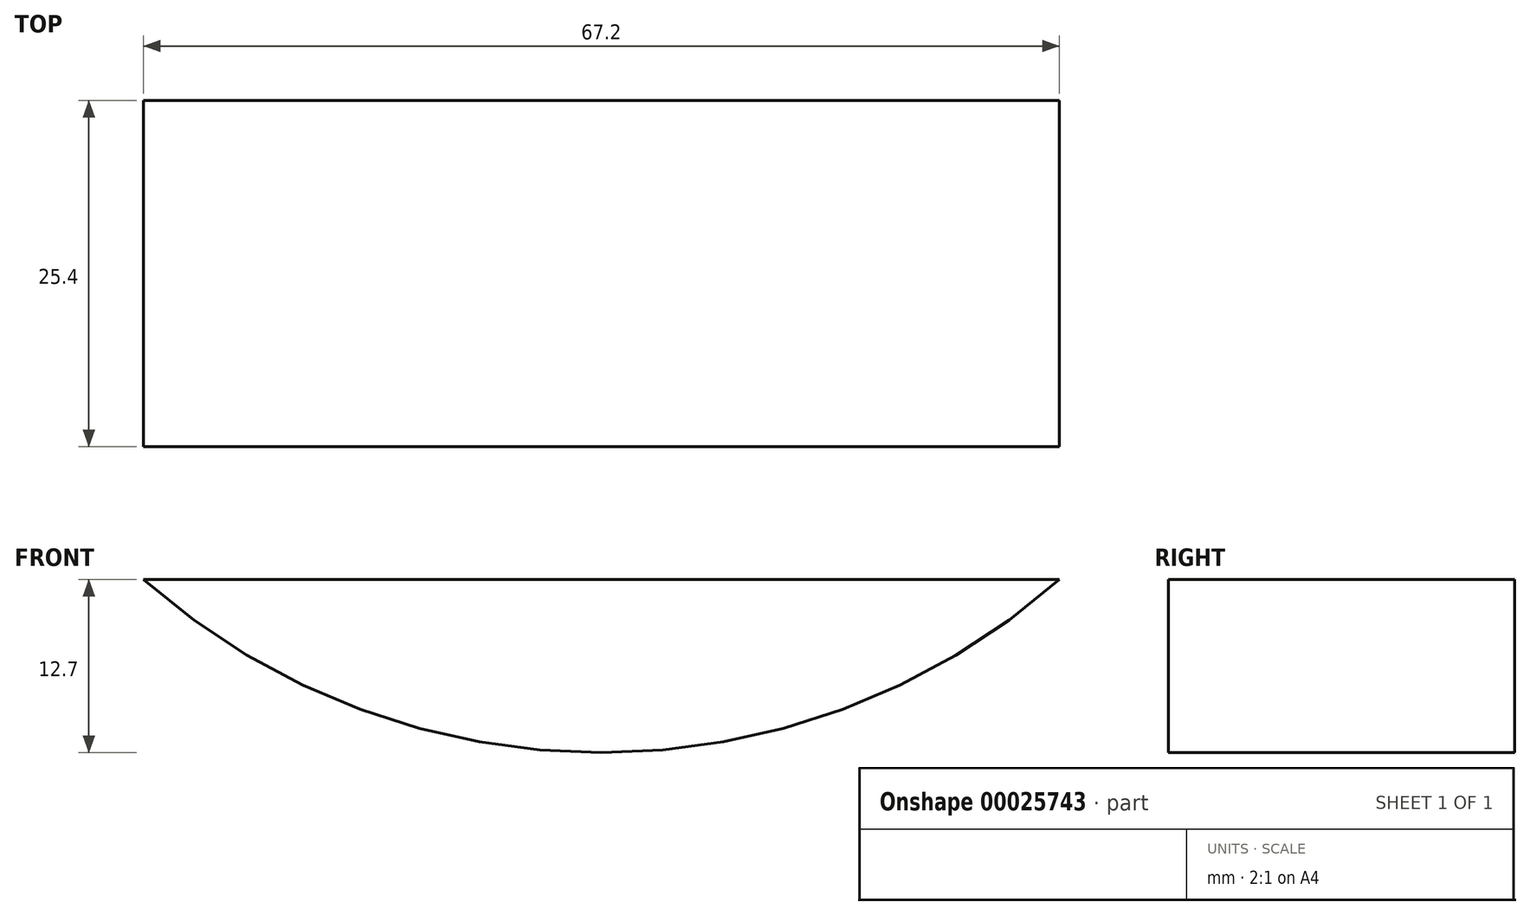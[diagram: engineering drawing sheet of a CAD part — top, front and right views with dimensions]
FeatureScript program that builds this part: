
annotation { "Feature Type Name" : "Feature", "Feature Type Description" : "" }
export const myFeature = defineFeature(function(context is Context, id is Id, definition is map)
    precondition{}
    {
        {
            var Q0;
            Q0=qCreatedBy(makeId("Front.planeOp"),FACE);
            var sketch = newSketch(context, id + "F0", { "sketchPlane" : qUnion([Q0])});
            skCircle(sketch, "E0", {"center": v(0, 0) * mm, "radius": 50.8 * mm});
            skLineSegment(sketch, "E1", {"start": v(0, -50.8) * mm, "end": v(139.61, -50.8) * mm});
            skCircle(sketch, "E2", {"center": v(84.02, 38.1) * mm, "radius": 38.1 * mm});
            skLineSegment(sketch, "E3", {"start": v(139.2, -38.1) * mm, "end": v(-114.53, -38.1) * mm});
            skSolve(sketch);
        }
        {
            var Q0;
            {var subQ0=sQuery(id+"F0.wireOp",EDGE,"E3");var subQ1=sQuery(id+"F0.wireOp",EDGE,"E0");var subQ3=makeQuery(id+"F0.imprint","INTERSECT",VERTEX,{"disambiguationData":[OD(0.0)],"derivedFrom":[subQ1,subQ0]});Q0=makeQuery(id+"F0.imprint","IMPRINT",FACE,{"disambiguationData":[TD([[makeQuery(id+"F0.imprint","IMPRINT",EDGE,{"disambiguationData":[TD([[subQ3,1.0]])],"derivedFrom":subQ1}),1.0]])]});}
            var Q1;
            {var subQ1=sQuery(id+"F0.wireOp",EDGE,"E0");var subQ4=makeQuery(id+"F0.imprint","IMPRINT",VERTEX,{"derivedFrom":subQ1});Q1=makeQuery(id+"F0.imprint","IMPRINT",FACE,{"disambiguationData":[TD([[makeQuery(id+"F0.imprint","IMPRINT",EDGE,{"disambiguationData":[TD([[subQ4,1.0]])],"derivedFrom":subQ1}),1.0]])]});}
            extrude(context, id + "F1", {"entities" : qUnion([Q0, Q1]), "depth" : 25.4 * mm});
        }
    });
